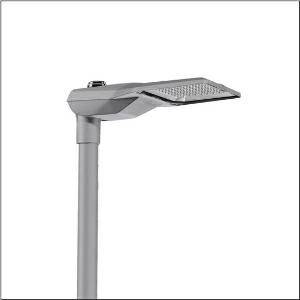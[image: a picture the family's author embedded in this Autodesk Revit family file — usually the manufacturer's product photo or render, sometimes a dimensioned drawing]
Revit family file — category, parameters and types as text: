
# Revit family: streetlight_sl_21_midi___st1_0a_5xe7d37n08mb_3723
name_source: partatom
category: Lighting Fixtures
units: mm (PartAtom-declared; Revit-internal decimal feet)

## family parameters
Cut with Voids When Loaded = No
Host = Face
Light Source = No
Part Type = Normal
Room Calculation Point = No
Round Connector Dimension = Use Diameter
Shared = No

## types (1)
- --- (1 x LED, 18270 lm, 136 W, 3000K)
    Apparent Load = 136 VA
    CIE Flux Codes = 37 72 97 100 100
    Color Rendering = 70
    Color Temperature = 3000K
    Default Elevation = 1800 mm
    Description = Streetlight SL 21 midi, mast luminaire, primary light control with lens, of PMMA, primary optical cover: cover, of toughened safety glass, transparent, light distribution: ST1.0a, light emission: direct distribution, primary light characteristic: asymmetric, installation type: side-entry, LED, 3G 2.5mm², High Power LED, rated luminous flux: 18.270lm, luminous efficacy: 134lm/W, light colour: 730, colour temperature: 3000K, control: overheat protection, pre-setting: linear dimming characteristic, constant luminous flux control, time-dependent luminous flux control, flexible luminous flux parameterisation, mains connection: 220..240V, AC, 50/60Hz, connection cable pre-assembled, cable length: 12,5m, wiring characteristics: H05VV-F, start of lifetime: 136W, end of service life: 142W, reduction: 61W, luminaire housing, of diecast aluminium (EN AC-44300), powder-coated, Siteco® metallic grey (DB 702S), corrosivity category C5 mid according to DIN EN ISO 12944, multi-level sealing system, sealing non-destructively replaceable, inclination adjustable: 0°, 5°, 10°, 15°, length: 644mm, width: 335mm, height: 110mm, spigot size: 42mm (side-entry), protection rating (complete): IP66, insulation class (complete): insulation class I (protective earthing), certification: CE, ENEC, ENEC+, VDE, impact resistance: IK09, permissible operating ambient temperature for outdoor applications: -40..+50°C, standard-compliant lighting for roads and squares, packaging unit: 1 piece

Light Distribution: ST1.0a
    Height = 111 mm
    Lamp = 1 x LED
    Lamp Light Flux = 18270 lm
    Lamp Power = 136 W
    Lamp count = 1
    Length = 644 mm
    Luminous efficacy = 134 lm/W
    Manufacturer = Siteco
    ModVariant = No
    Model = 5XE7D37N08MB
    Number of Poles = 1
    OnlyDefault = Yes
    Power Factor = 1
    Product Name = Streetlight SL 21 midi | ST1.0a
    Product group = mast luminaire | pylon top
    ProductGroupID = 6100
    Protection Class = Protection class I
    Protection Degree = IP 66
    RLX_Detail_Level = 1
    RLX_Emergency_Light_Flux = 0 lm
    RLX_Emergency_Type = 0
    RLX_Emergency_Type_DB = No
    RlxData = <blob elided: 90629 chars, md5=ac23d043>
    Socket = socket
    Standby Power = 0 W
    System Light Flux = 18270 lm
    System Power = 136 W
    Type Comments = factory setting: luminous flux: 100 % | dim-lin: 254 | 695 mA
    Type Image = l_1294377.jpg
    URL = http://relux.com
    VarID = @adj_105851
    Voltage = 0 V
    Weight = 0.00 kg
    Width = 336 mm

## geometry (parser evidence)
native form markers: Blend x4, Sweep x10
no freeform markers — native parametric forms only
